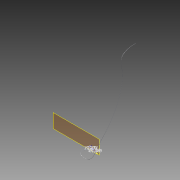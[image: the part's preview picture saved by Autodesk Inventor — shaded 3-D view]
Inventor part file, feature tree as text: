
AUTODESK INVENTOR PART (.ipt)
format: ipt  version: 2012 (Build 160160000, 160)  size: 113,664 bytes
history: native  units: in
note: dims shown in document units (in); Inventor stores cm internally (conversion verified against a paired STEP export)
features: sketch x3, plane x2, sweep x1
ambient origin geometry x8: Origin, YZ Plane, XZ Plane, XY Plane, X Axis, Y Axis, Z Axis, Center Point
bodies: Solid1 (feature_tree)
feature tree (6):
  plane  "Work Plane1"
  sketch  "Sketch3"  dims[d1=1.4641in d2=2.2579in]
  sketch  "3D Sketch2"
  plane  "Work Plane2"
  sweep  "Sweep1"
  sketch  "Sketch4"  dims[d3=0.8728in d4=0.7523in d5=0.0787in d6=0.0in]
